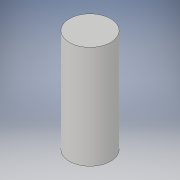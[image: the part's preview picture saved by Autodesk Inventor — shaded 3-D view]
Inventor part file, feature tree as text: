
AUTODESK INVENTOR PART (.ipt)
format: ipt  version: 2019 (Build 230136000, 136)  size: 208,384 bytes
history: native  units: mm
features: extrude x1, sketch x1
ambient origin geometry x8: Origin, YZ Plane, XZ Plane, XY Plane, X Axis, Y Axis, Z Axis, Center Point
bodies: Solid1 (feature_tree)
feature tree (2):
  extrude  "Extrusion1"  Depth=20.0mm TaperAngle=0.0deg
  sketch  "Sketch1"  dims[d0=8.0mm d1=20.0mm d2=0.0mm]
